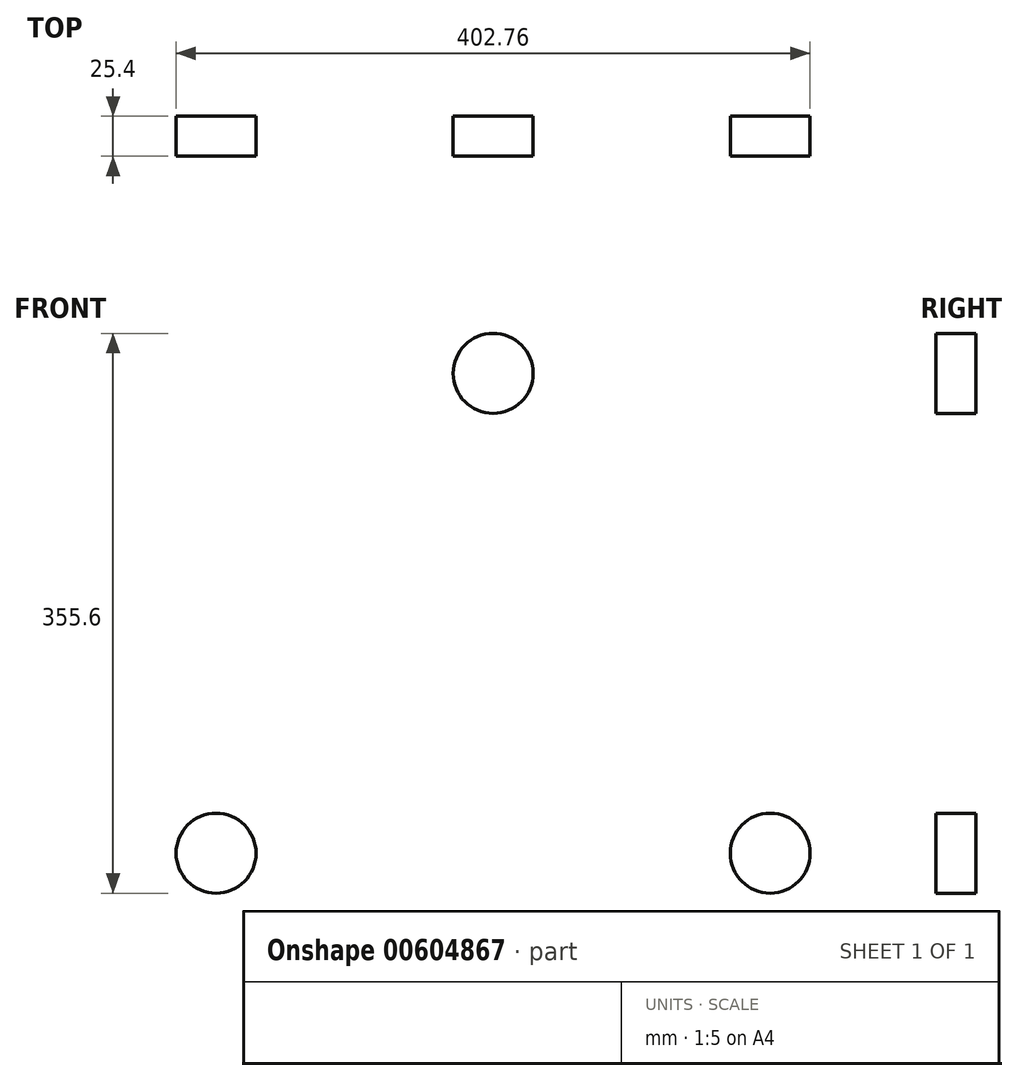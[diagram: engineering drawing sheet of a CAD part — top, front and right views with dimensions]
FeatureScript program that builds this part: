
annotation { "Feature Type Name" : "Feature", "Feature Type Description" : "" }
export const myFeature = defineFeature(function(context is Context, id is Id, definition is map)
    precondition{}
    {
        {
            var Q0;
            Q0=qCreatedBy(makeId("Front.planeOp"),FACE);
            var sketch = newSketch(context, id + "F0", { "sketchPlane" : qUnion([Q0])});
            skCircle(sketch, "E0", {"center": v(0, 203.2) * mm, "radius": 25.4 * mm});
            skCircle(sketch, "E1.1.0", {"center": v(175.98, -101.6) * mm, "radius": 25.4 * mm});
            skCircle(sketch, "E1.2.0", {"center": v(-175.98, -101.6) * mm, "radius": 25.4 * mm});
            skPoint(sketch, "E1.center", {"position": v(0, 0) * mm});
            skLineSegment(sketch, "E1.anchor1", {"start": v(0, 0) * mm, "end": v(0, 203.2) * mm, "construction": true});
            skLineSegment(sketch, "E1.anchor2", {"start": v(0, 0) * mm, "end": v(-175.98, -101.6) * mm, "construction": true});
            skSolve(sketch);
        }
        {
            var Q0;
            Q0=makeQuery(id+"F0.imprint","IMPRINT",FACE,{"disambiguationData":[TD([[makeQuery(id+"F0.imprint","IMPRINT",EDGE,{"derivedFrom":sQuery(id+"F0.wireOp",EDGE,"E0")}),1.0]])]});
            var Q1;
            Q1=makeQuery(id+"F0.imprint","IMPRINT",FACE,{"disambiguationData":[TD([[makeQuery(id+"F0.imprint","IMPRINT",EDGE,{"derivedFrom":sQuery(id+"F0.wireOp",EDGE,"E1.1.0")}),1.0]])]});
            var Q2;
            Q2=makeQuery(id+"F0.imprint","IMPRINT",FACE,{"disambiguationData":[TD([[makeQuery(id+"F0.imprint","IMPRINT",EDGE,{"derivedFrom":sQuery(id+"F0.wireOp",EDGE,"E1.2.0")}),1.0]])]});
            extrude(context, id + "F1", {"entities" : qUnion([Q0, Q1, Q2]), "depth" : 25.4 * mm, "offsetDistance" : 25.4 * mm});
        }
    });
